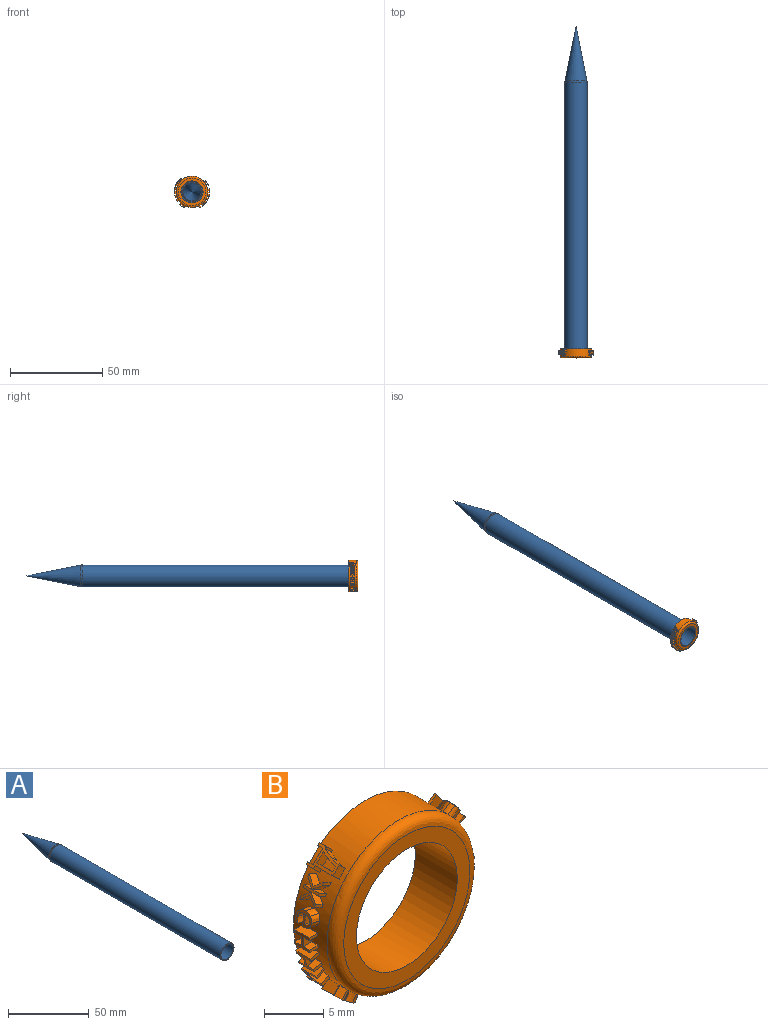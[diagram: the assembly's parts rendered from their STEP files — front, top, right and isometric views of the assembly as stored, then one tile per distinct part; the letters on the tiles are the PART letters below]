
ASSEMBLY  parts=2 mates=1
PART A: 8 faces, bbox 12x180x12 mm
  f0: cylinder r=5.5mm len=150mm, axis (0,1,0), area 5183.6mm2, adj f2,f4
  f1: cylinder r=6mm len=149.51mm, axis (0,1,0), area 5636.2mm2, adj f2,f5
  f2: plane 12x12mm, normal (0,-1,0), area 18.1mm2, adj f0,f1
  f3: cone r=6mm half-angle=11.3deg, axis (0,-1,0), area 558.2mm2, adj f5
  f4: plane 11x11mm, normal (0,-1,0), area 17.5mm2, adj f0,f6
  f5: torus R=1mm, axis (0,-1,0), area 37mm2, adj f1,f3
  f6: torus R=1mm, axis (0,-1,0), area 9.1mm2, adj f4,f7
  f7: cone r=5.02mm half-angle=11.3deg, axis (0,-1,0), area 388.1mm2, adj f6
PART B: 300 faces, bbox 19x5x17.5 mm
  f0: plane 2.34x0.87mm, normal (0.87,0,0.49), area 2.3mm2, adj f1,f9,f10,f32
  f1: plane 1.01x0.73mm, normal (0,-1,0), area 0.3mm2, adj f0,f2,f10,f32
  f2: plane 2.36x0.87mm, normal (-0.87,0,-0.49), area 2.4mm2, adj f1,f3,f10,f32
  f3: extruded ~0.92x0.56mm, area 0.3mm2, adj f2,f4,f10,f32
  f4: extruded ~1x0.7mm, area 0.3mm2, adj f3,f5,f10,f32
  f5: extruded ~1x0.7mm, area 0.2mm2, adj f4,f6,f10,f32
  f6: plane 0.88x0.49mm, normal (-0.87,0,-0.49), area 0.2mm2, adj f5,f7,f10,f32
  f7: extruded ~1x0.7mm, area 0.2mm2, adj f6,f8,f10,f32
  f8: extruded ~1.1x0.88mm, area 0.5mm2, adj f7,f9,f10,f32
  f9: extruded ~0.95x0.62mm, area 0.5mm2, adj f0,f8,f10,f32
  f10: cylinder r=9.5mm len=2.98mm, axis (0,1,0), area 0.9mm2, adj f0,f1,f2,f3,f4,f5,f6,f7
  f11: extruded ~0.95x0.86mm, area 0.3mm2, adj f12,f24,f30,f32
  f12: extruded ~0.97x0.88mm, area 0.3mm2, adj f11,f13,f30,f32
  f13: extruded ~1.18x1.13mm, area 0.7mm2, adj f12,f14,f30,f32
  f14: extruded ~0.93x0.83mm, area 0.7mm2, adj f13,f15,f30,f32
  f15: extruded ~0.92x0.82mm, area 0.7mm2, adj f14,f16,f30,f32
  f16: extruded ~1.14x1.09mm, area 0.6mm2, adj f15,f17,f30,f32
  f17: extruded ~1.12x1.06mm, area 0.6mm2, adj f16,f18,f30,f32
  f18: extruded ~0.9x0.8mm, area 0.6mm2, adj f17,f19,f30,f32
  f19: plane 0.77x0.64mm, normal (0.77,0,0.64), area 0.2mm2, adj f18,f20,f30,f32
  f20: plane 1.57x1.56mm, normal (0,1,0), area 1.2mm2, adj f19,f21,f30,f32
  f21: extruded ~0.87x0.77mm, area 0.5mm2, adj f20,f22,f30,f32
  f22: extruded ~1.04x0.97mm, area 0.5mm2, adj f21,f23,f30,f32
  f23: extruded ~1.15x1.09mm, area 0.6mm2, adj f22,f24,f30,f32
  f24: plane 0.77x0.64mm, normal (0.77,0,0.64), area 0.2mm2, adj f11,f23,f30,f32
  f25: plane 1.36x1.35mm, normal (0,-1,0), area 0.9mm2, adj f26,f29,f30,f31
  f26: extruded ~0.87x0.76mm, area 0.4mm2, adj f25,f27,f30,f31
  f27: extruded ~0.99x0.91mm, area 0.4mm2, adj f26,f28,f30,f31
  f28: extruded ~0.98x0.89mm, area 0.4mm2, adj f27,f29,f30,f31
  f29: extruded ~0.84x0.73mm, area 0.4mm2, adj f25,f28,f30,f31
  f30: cylinder r=9.5mm len=1.83mm, axis (0,1,0), area 1.2mm2, adj f11,f12,f13,f14,f15,f16,f17,f18
  f31: cylinder r=8.5mm len=0.71mm, axis (0,1,0), area 0.4mm2, adj f25,f26,f27,f28,f29
  f32: cylinder r=8.5mm len=17mm, axis (0,1,0), area 190.6mm2, adj f0,f1,f2,f3,f4,f5,f6,f7
  f33: plane 1.21x0.79mm, normal (0.61,0,0.79), area 1.2mm2, adj f32,f34,f51,f60
  f34: plane 0.91x0.78mm, normal (0,1,0), area 0.2mm2, adj f32,f33,f35,f60
  f35: plane 0.82x0.66mm, normal (-0.6,0.21,-0.77), area 0.3mm2, adj f32,f34,f36,f60
  f36: plane 0.8x0.62mm, normal (0,1,0), area 0mm2, adj f32,f35,f37,f60
  f37: extruded ~0.96x0.83mm, area 0.4mm2, adj f32,f36,f38,f60
  f38: extruded ~0.99x0.87mm, area 0.3mm2, adj f32,f37,f39,f60
  f39: extruded ~1.06x0.95mm, area 0.4mm2, adj f32,f38,f40,f60
  f40: extruded ~0.89x0.74mm, area 0.4mm2, adj f32,f39,f41,f60
  f41: extruded ~1.34x1.31mm, area 1.2mm2, adj f32,f40,f42,f60
  f42: plane 0.97x0.85mm, normal (-0.02,-1,-0.03), area 0.3mm2, adj f32,f41,f43,f60
  f43: plane 0.79x0.61mm, normal (-0.61,0,-0.79), area 0.1mm2, adj f32,f42,f44,f60
  f44: extruded ~0.85x0.68mm, area 0.3mm2, adj f32,f43,f45,f60
  f45: extruded ~0.97x0.84mm, area 0.3mm2, adj f32,f44,f46,f60
  f46: extruded ~1.11x1.01mm, area 0.5mm2, adj f32,f45,f47,f60
  f47: plane 0.85x0.67mm, normal (-0.57,0.37,-0.73), area 0.2mm2, adj f32,f46,f48,f60
  f48: extruded ~0.98x0.85mm, area 0.3mm2, adj f32,f47,f49,f60
  f49: extruded ~0.99x0.86mm, area 0.3mm2, adj f32,f48,f50,f60
  f50: extruded ~1.09x0.99mm, area 0.5mm2, adj f32,f49,f51,f60
  f51: extruded ~0.9x0.74mm, area 0.5mm2, adj f32,f33,f50,f60
  f52: extruded ~0.88x0.73mm, area 0.3mm2, adj f53,f59,f60,f61
  f53: extruded ~1.08x0.98mm, area 0.5mm2, adj f52,f54,f60,f61
  f54: plane 0.95x0.83mm, normal (0.02,1,0.03), area 0.3mm2, adj f53,f55,f60,f61
  f55: plane 0.79x0.61mm, normal (-0.61,0,-0.79), area 0.2mm2, adj f54,f56,f60,f61
  f56: extruded ~0.88x0.73mm, area 0.4mm2, adj f55,f57,f60,f61
  f57: extruded ~1.03x0.92mm, area 0.4mm2, adj f56,f58,f60,f61
  f58: extruded ~0.95x0.81mm, area 0.3mm2, adj f57,f59,f60,f61
  f59: extruded ~0.85x0.68mm, area 0.2mm2, adj f52,f58,f60,f61
  f60: cylinder r=9.5mm len=1.83mm, axis (0,1,0), area 1.2mm2, adj f33,f34,f35,f36,f37,f38,f39,f40
  f61: cylinder r=8.5mm len=0.69mm, axis (0,1,0), area 0.4mm2, adj f52,f53,f54,f55,f56,f57,f58,f59
  f62: extruded ~0.99x0.58mm, area 0.5mm2, adj f32,f63,f78,f79
  f63: extruded ~1.13x0.87mm, area 0.5mm2, adj f32,f62,f64,f79
  f64: extruded ~1.05x0.72mm, area 0.3mm2, adj f32,f63,f65,f79
  f65: extruded ~1.01x0.64mm, area 0.3mm2, adj f32,f64,f66,f79
  f66: plane 0.91x0.43mm, normal (0,-1,0), area 0mm2, adj f32,f65,f67,f79
  f67: plane 0.93x0.46mm, normal (0.42,-0.18,0.89), area 0.2mm2, adj f32,f66,f68,f79
  f68: plane 1.01x0.61mm, normal (0,-1,0), area 0.2mm2, adj f32,f67,f69,f79
  f69: plane 1.77x0.91mm, normal (-0.42,0,-0.91), area 1.8mm2, adj f32,f68,f70,f79
  f70: plane 1.04x0.66mm, normal (0,1,0), area 0.3mm2, adj f32,f69,f71,f79
  f71: plane 0.93x0.91mm, normal (0.42,0,0.91), area 0.9mm2, adj f32,f70,f72,f79
  f72: extruded ~0.97x0.54mm, area 0.5mm2, adj f32,f71,f73,f79
  f73: extruded ~1.08x0.79mm, area 0.4mm2, adj f32,f72,f74,f79
  f74: extruded ~1.05x0.71mm, area 0.3mm2, adj f32,f73,f75,f79
  f75: extruded ~0.95x0.51mm, area 0.3mm2, adj f32,f74,f76,f79
  f76: plane 1.14x0.91mm, normal (-0.42,0,-0.91), area 1.1mm2, adj f32,f75,f77,f79
  f77: plane 1x0.67mm, normal (0,1,0), area 0.3mm2, adj f32,f76,f78,f79
  f78: plane 1.15x0.91mm, normal (0.42,0,0.91), area 1.2mm2, adj f32,f62,f77,f79
  f79: cylinder r=9.5mm len=1.8mm, axis (0,1,0), area 1.1mm2, adj f62,f63,f64,f65,f66,f67,f68,f69
  f80: extruded ~1.03x0.49mm, area 0.5mm2, adj f32,f81,f96,f97
  f81: extruded ~1.1x0.68mm, area 0.5mm2, adj f32,f80,f82,f97
  f82: extruded ~1.05x0.53mm, area 0.3mm2, adj f32,f81,f83,f97
  f83: extruded ~1.03x0.43mm, area 0.3mm2, adj f32,f82,f84,f97
  f84: plane 0.98x0.21mm, normal (0,-1,0), area 0mm2, adj f32,f83,f85,f97
  f85: plane 0.99x0.24mm, normal (0.2,-0.18,0.96), area 0.2mm2, adj f32,f84,f86,f97
  f86: plane 1.04x0.41mm, normal (0,-1,0), area 0.2mm2, adj f32,f85,f87,f97
  f87: plane 1.77x0.98mm, normal (-0.2,0,-0.98), area 1.8mm2, adj f32,f86,f88,f97
  f88: plane 1.05x0.46mm, normal (0,1,0), area 0.3mm2, adj f32,f87,f89,f97
  f89: plane 0.98x0.93mm, normal (0.2,0,0.98), area 0.9mm2, adj f32,f88,f90,f97
  f90: extruded ~1.01x0.5mm, area 0.5mm2, adj f32,f89,f91,f97
  f91: extruded ~1.07x0.6mm, area 0.4mm2, adj f32,f90,f92,f97
  f92: extruded ~1.05x0.51mm, area 0.3mm2, adj f32,f91,f93,f97
  f93: extruded ~1.01x0.32mm, area 0.3mm2, adj f32,f92,f94,f97
  f94: plane 1.14x0.98mm, normal (-0.2,0,-0.98), area 1.1mm2, adj f32,f93,f95,f97
  f95: plane 1.02x0.47mm, normal (0,1,0), area 0.3mm2, adj f32,f94,f96,f97
  f96: plane 1.15x0.98mm, normal (0.2,0,0.98), area 1.2mm2, adj f32,f80,f95,f97
  f97: cylinder r=9.5mm len=1.8mm, axis (0,1,0), area 1.1mm2, adj f80,f81,f82,f83,f84,f85,f86,f87
  f98: plane 1.77x1mm, normal (-0.04,0,-1), area 1.8mm2, adj f32,f99,f101,f102
  f99: plane 1.01x0.31mm, normal (0,1,0), area 0.3mm2, adj f32,f98,f100,f102
  f100: plane 1.77x1mm, normal (0.04,0,1), area 1.8mm2, adj f32,f99,f101,f102
  f101: plane 1.01x0.31mm, normal (0,-1,0), area 0.3mm2, adj f32,f98,f100,f102
  f102: cylinder r=9.5mm len=1.77mm, axis (0,1,0), area 0.5mm2, adj f98,f99,f100,f101
  f103: extruded ~1.01x0.15mm, area 0.1mm2, adj f32,f104,f110,f111
  f104: extruded ~1x0.13mm, area 0.1mm2, adj f32,f103,f105,f111
  f105: extruded ~1x0.13mm, area 0.1mm2, adj f32,f104,f106,f111
  f106: extruded ~1.01x0.15mm, area 0.1mm2, adj f32,f105,f107,f111
  f107: extruded ~1x0.15mm, area 0.1mm2, adj f32,f106,f108,f111
  f108: extruded ~1x0.13mm, area 0.1mm2, adj f32,f107,f109,f111
  f109: extruded ~1x0.13mm, area 0.1mm2, adj f32,f108,f110,f111
  f110: extruded ~1x0.15mm, area 0.1mm2, adj f32,f103,f109,f111
  f111: cylinder r=9.5mm len=0.36mm, axis (0,1,0), area 0.1mm2, adj f103,f104,f105,f106,f107,f108,f109,f110
  f112: extruded ~1.04x0.39mm, area 0.3mm2, adj f32,f113,f125,f131
  f113: extruded ~1.04x0.42mm, area 0.3mm2, adj f32,f112,f114,f131
  f114: extruded ~1.08x0.73mm, area 0.7mm2, adj f32,f113,f115,f131
  f115: extruded ~1.04x0.66mm, area 0.7mm2, adj f32,f114,f116,f131
  f116: extruded ~1.04x0.68mm, area 0.7mm2, adj f32,f115,f117,f131
  f117: extruded ~1.08x0.68mm, area 0.6mm2, adj f32,f116,f118,f131
  f118: extruded ~1.07x0.64mm, area 0.6mm2, adj f32,f117,f119,f131
  f119: extruded ~1.03x0.58mm, area 0.6mm2, adj f32,f118,f120,f131
  f120: plane 1x0.17mm, normal (-0.12,0,0.99), area 0.2mm2, adj f32,f119,f121,f131
  f121: plane 1.33x1.16mm, normal (0,1,0), area 1.2mm2, adj f32,f120,f122,f131
  f122: extruded ~1.02x0.47mm, area 0.5mm2, adj f32,f121,f123,f131
  f123: extruded ~1.05x0.54mm, area 0.5mm2, adj f32,f122,f124,f131
  f124: extruded ~1.08x0.68mm, area 0.6mm2, adj f32,f123,f125,f131
  f125: plane 1x0.24mm, normal (-0.12,0,0.99), area 0.2mm2, adj f32,f112,f124,f131
  f126: plane 1.1x1.04mm, normal (0,-1,0), area 0.9mm2, adj f127,f130,f131,f132
  f127: extruded ~1.02x0.38mm, area 0.4mm2, adj f126,f128,f131,f132
  f128: extruded ~1.04x0.46mm, area 0.4mm2, adj f127,f129,f131,f132
  f129: extruded ~1.04x0.44mm, area 0.4mm2, adj f128,f130,f131,f132
  f130: extruded ~1.01x0.39mm, area 0.4mm2, adj f126,f129,f131,f132
  f131: cylinder r=9.5mm len=1.83mm, axis (0,1,0), area 1.2mm2, adj f112,f113,f114,f115,f116,f117,f118,f119
  f132: cylinder r=8.5mm len=0.92mm, axis (0,1,0), area 0.4mm2, adj f126,f127,f128,f129,f130
  f133: plane 1.17x1mm, normal (0.26,-0.79,-0.55), area 0.8mm2, adj f32,f134,f141,f142
  f134: plane 0.96x0.56mm, normal (0.34,0.61,-0.71), area 0.2mm2, adj f32,f133,f135,f142
  f135: extruded ~1.07x0.78mm, area 0.5mm2, adj f32,f134,f136,f142
  f136: extruded ~0.94x0.5mm, area 0.1mm2, adj f32,f135,f137,f142
  f137: extruded ~0.91x0.44mm, area 0.4mm2, adj f32,f136,f138,f142
  f138: plane 1.68x0.9mm, normal (0.43,0,-0.9), area 1.7mm2, adj f32,f137,f139,f142
  f139: plane 1.03x0.66mm, normal (0,1,0), area 0.3mm2, adj f32,f138,f140,f142
  f140: plane 2.36x0.9mm, normal (-0.43,0,0.9), area 2.4mm2, adj f32,f139,f141,f142
  f141: plane 1.01x0.63mm, normal (0,-1,0), area 0.2mm2, adj f32,f133,f140,f142
  f142: cylinder r=9.5mm len=2.36mm, axis (0,1,0), area 0.8mm2, adj f133,f134,f135,f136,f137,f138,f139,f140
  f143: plane 0.8x0.6mm, normal (-0.6,0,0.8), area 0mm2, adj f32,f144,f162,f163
  f144: plane 1.1x1.02mm, normal (-0.42,0.71,0.56), area 0.7mm2, adj f32,f143,f145,f163
  f145: extruded ~1.1x0.98mm, area 0.7mm2, adj f32,f144,f146,f163
  f146: extruded ~0.89x0.7mm, area 0.5mm2, adj f32,f145,f147,f163
  f147: extruded ~0.93x0.76mm, area 0.5mm2, adj f32,f146,f148,f163
  f148: extruded ~1.12x1.02mm, area 0.6mm2, adj f32,f147,f149,f163
  f149: extruded ~1.25x1.19mm, area 0.8mm2, adj f32,f148,f150,f163
  f150: plane 0.88x0.72mm, normal (0.47,0.61,-0.63), area 0.2mm2, adj f32,f149,f151,f163
  f151: extruded ~0.99x0.84mm, area 0.3mm2, adj f32,f150,f152,f163
  f152: extruded ~0.97x0.82mm, area 0.3mm2, adj f32,f151,f153,f163
  f153: extruded ~1x0.85mm, area 0.3mm2, adj f32,f152,f154,f163
  f154: extruded ~0.88x0.69mm, area 0.3mm2, adj f32,f153,f155,f163
  f155: extruded ~0.83x0.63mm, area 0.3mm2, adj f32,f154,f156,f163
  f156: extruded ~0.89x0.71mm, area 0.3mm2, adj f32,f155,f157,f163
  f157: extruded ~1.03x0.9mm, area 0.6mm2, adj f32,f156,f158,f163
  f158: plane 1.15x1.12mm, normal (0.42,-0.71,-0.57), area 0.9mm2, adj f32,f157,f159,f163
  f159: plane 0.81x0.6mm, normal (0.6,0,-0.8), area 0.2mm2, adj f32,f158,f160,f163
  f160: plane 1.85x1.73mm, normal (0,1,0), area 1.6mm2, adj f32,f159,f161,f163
  f161: plane 0.81x0.6mm, normal (-0.6,0,0.8), area 0.2mm2, adj f32,f160,f162,f163
  f162: plane 1.56x1.54mm, normal (0,-1,0), area 1.2mm2, adj f32,f143,f161,f163
  f163: cylinder r=9.5mm len=2.39mm, axis (0,1,0), area 1.2mm2, adj f143,f144,f145,f146,f147,f148,f149,f150
  f164: plane 0.93x0.91mm, normal (0,-1,0), area 0.3mm2, adj f32,f165,f176,f182
  f165: plane 0.86x0.72mm, normal (-0.7,0,-0.72), area 0.9mm2, adj f32,f164,f166,f182
  f166: plane 0.91x0.88mm, normal (0,1,0), area 0.3mm2, adj f32,f165,f167,f182
  f167: plane 0.72x0.7mm, normal (0.7,0,0.72), area 0.6mm2, adj f32,f166,f168,f182
  f168: plane 1.88x1.86mm, normal (0,1,0), area 1.6mm2, adj f32,f167,f169,f182
  f169: plane 0.72x0.7mm, normal (-0.7,0,-0.72), area 0.6mm2, adj f32,f168,f170,f182
  f170: plane 0.93x0.87mm, normal (0,1,0), area 0.3mm2, adj f32,f169,f171,f182
  f171: plane 0.86x0.72mm, normal (0.7,0,0.72), area 0.9mm2, adj f32,f170,f172,f182
  f172: plane 0.87x0.82mm, normal (0,-1,0), area 0.2mm2, adj f32,f171,f173,f182
  f173: extruded ~1.04x1.03mm, area 1.1mm2, adj f32,f172,f174,f182
  f174: extruded ~1.09x0.86mm, area 1.1mm2, adj f32,f173,f175,f182
  f175: plane 1.47x1.44mm, normal (0,-1,0), area 1.1mm2, adj f32,f174,f176,f182
  f176: plane 2.11x0.72mm, normal (-0.7,0,-0.72), area 2.1mm2, adj f32,f164,f175,f182
  f177: extruded ~0.94x0.86mm, area 1mm2, adj f178,f181,f182,f183
  f178: plane 1.09x1.09mm, normal (0,1,0), area 0.5mm2, adj f177,f179,f182,f183
  f179: plane 1.86x0.72mm, normal (0.7,0,0.72), area 1.9mm2, adj f178,f180,f182,f183
  f180: plane 1.51x1.49mm, normal (0,-1,0), area 1.1mm2, adj f179,f181,f182,f183
  f181: extruded ~1x0.99mm, area 1mm2, adj f177,f180,f182,f183
  f182: cylinder r=9.5mm len=2.97mm, axis (0,1,0), area 2.2mm2, adj f164,f165,f166,f167,f168,f169,f170,f171
  f183: cylinder r=8.5mm len=1.86mm, axis (0,1,0), area 1.5mm2, adj f177,f178,f179,f180,f181
  f184: plane 1.27x1.09mm, normal (-0.35,-0.65,-0.68), area 1.1mm2, adj f32,f185,f201,f202
  f185: plane 0.89x0.86mm, normal (0.46,0,0.89), area 0.9mm2, adj f32,f184,f186,f202
  f186: plane 1.01x0.68mm, normal (0,-1,0), area 0.2mm2, adj f32,f185,f187,f202
  f187: plane 0.89x0.86mm, normal (-0.46,0,-0.89), area 0.9mm2, adj f32,f186,f188,f202
  f188: plane 1.2x1.12mm, normal (0.35,-0.65,0.68), area 1.1mm2, adj f32,f187,f189,f202
  f189: plane 1x0.73mm, normal (0,-1,0), area 0.3mm2, adj f32,f188,f190,f202
  f190: plane 1.18x1.14mm, normal (-0.35,0.65,-0.67), area 1.1mm2, adj f32,f189,f191,f202
  f191: plane 1.21x1.2mm, normal (-0.34,-0.66,-0.67), area 1.2mm2, adj f32,f190,f192,f202
  f192: plane 1.01x0.75mm, normal (0,1,0), area 0.3mm2, adj f32,f191,f193,f202
  f193: plane 1.22x1.17mm, normal (0.35,0.66,0.67), area 1.2mm2, adj f32,f192,f194,f202
  f194: plane 0.9x0.89mm, normal (-0.46,0,-0.89), area 0.9mm2, adj f32,f193,f195,f202
  f195: plane 1.01x0.68mm, normal (0,1,0), area 0.2mm2, adj f32,f194,f196,f202
  f196: plane 0.9x0.89mm, normal (0.46,0,0.89), area 0.9mm2, adj f32,f195,f197,f202
  f197: plane 1.3x1.13mm, normal (-0.35,0.66,-0.67), area 1.2mm2, adj f32,f196,f198,f202
  f198: plane 1.07x0.72mm, normal (0,1,0), area 0.3mm2, adj f32,f197,f199,f202
  f199: plane 1.34x1.14mm, normal (0.34,-0.66,0.67), area 1.2mm2, adj f32,f198,f200,f202
  f200: plane 1.3x1.08mm, normal (0.35,0.65,0.67), area 1.1mm2, adj f32,f199,f201,f202
  f201: plane 1.06x0.71mm, normal (0,-1,0), area 0.3mm2, adj f32,f184,f200,f202
  f202: cylinder r=9.5mm len=2.14mm, axis (0,1,0), area 1.5mm2, adj f184,f185,f186,f187,f188,f189,f190,f191
  f203: extruded ~1.05x0.47mm, area 0.3mm2, adj f32,f204,f216,f222
  f204: extruded ~1.05x0.51mm, area 0.3mm2, adj f32,f203,f205,f222
  f205: extruded ~1.12x0.82mm, area 0.7mm2, adj f32,f204,f206,f222
  f206: extruded ~1.04x0.66mm, area 0.7mm2, adj f32,f205,f207,f222
  f207: extruded ~1.04x0.68mm, area 0.7mm2, adj f32,f206,f208,f222
  f208: extruded ~1.11x0.76mm, area 0.6mm2, adj f32,f207,f209,f222
  f209: extruded ~1.1x0.72mm, area 0.6mm2, adj f32,f208,f210,f222
  f210: extruded ~1.03x0.58mm, area 0.6mm2, adj f32,f209,f211,f222
  f211: plane 0.98x0.21mm, normal (-0.21,0,-0.98), area 0.2mm2, adj f32,f210,f212,f222
  f212: plane 1.4x1.22mm, normal (0,1,0), area 1.2mm2, adj f32,f211,f213,f222
  f213: extruded ~1.02x0.47mm, area 0.5mm2, adj f32,f212,f214,f222
  f214: extruded ~1.07x0.62mm, area 0.5mm2, adj f32,f213,f215,f222
  f215: extruded ~1.12x0.76mm, area 0.6mm2, adj f32,f214,f216,f222
  f216: plane 0.98x0.24mm, normal (-0.21,0,-0.98), area 0.2mm2, adj f32,f203,f215,f222
  f217: plane 1.17x1.11mm, normal (0,-1,0), area 0.9mm2, adj f218,f221,f222,f223
  f218: extruded ~1.02x0.38mm, area 0.4mm2, adj f217,f219,f222,f223
  f219: extruded ~1.06x0.54mm, area 0.4mm2, adj f218,f220,f222,f223
  f220: extruded ~1.05x0.52mm, area 0.4mm2, adj f219,f221,f222,f223
  f221: extruded ~1.01x0.39mm, area 0.4mm2, adj f217,f220,f222,f223
  f222: cylinder r=9.5mm len=1.83mm, axis (0,1,0), area 1.2mm2, adj f203,f204,f205,f206,f207,f208,f209,f210
  f223: cylinder r=8.5mm len=0.9mm, axis (0,1,0), area 0.4mm2, adj f217,f218,f219,f220,f221
  f224: plane 1.01x0.29mm, normal (0,1,0), area 0.3mm2, adj f32,f225,f235,f236
  f225: plane 1x0.8mm, normal (0.02,0,-1), area 0.8mm2, adj f32,f224,f226,f236
  f226: plane 1.03x1.01mm, normal (0,1,0), area 1mm2, adj f32,f225,f227,f236
  f227: plane 1x0.8mm, normal (-0.02,0,1), area 0.8mm2, adj f32,f226,f228,f236
  f228: plane 1.03x0.29mm, normal (0,1,0), area 0.3mm2, adj f32,f227,f229,f236
  f229: plane 1.77x1mm, normal (0.02,0,-1), area 1.8mm2, adj f32,f228,f230,f236
  f230: plane 1.03x0.29mm, normal (0,-1,0), area 0.3mm2, adj f32,f229,f231,f236
  f231: plane 1x0.74mm, normal (-0.02,0,1), area 0.7mm2, adj f32,f230,f232,f236
  f232: plane 1.03x1.01mm, normal (0,-1,0), area 1mm2, adj f32,f231,f233,f236
  f233: plane 1x0.74mm, normal (0.02,0,-1), area 0.7mm2, adj f32,f232,f234,f236
  f234: plane 1.01x0.29mm, normal (0,-1,0), area 0.3mm2, adj f32,f233,f235,f236
  f235: plane 1.77x1mm, normal (-0.02,0,1), area 1.8mm2, adj f32,f224,f234,f236
  f236: cylinder r=9.5mm len=1.77mm, axis (0,1,0), area 1.2mm2, adj f224,f225,f226,f227,f228,f229,f230,f231
  f237: plane 1.02x0.52mm, normal (0,1,0), area 0.3mm2, adj f32,f238,f248,f249
  f238: plane 0.97x0.8mm, normal (0.26,0,-0.97), area 0.8mm2, adj f32,f237,f239,f249
  f239: plane 1.23x1.21mm, normal (0,1,0), area 1mm2, adj f32,f238,f240,f249
  f240: plane 0.97x0.8mm, normal (-0.26,0,0.97), area 0.8mm2, adj f32,f239,f241,f249
  f241: plane 1.06x0.51mm, normal (0,1,0), area 0.3mm2, adj f32,f240,f242,f249
  f242: plane 1.77x0.97mm, normal (0.26,0,-0.97), area 1.8mm2, adj f32,f241,f243,f249
  f243: plane 1.06x0.51mm, normal (0,-1,0), area 0.3mm2, adj f32,f242,f244,f249
  f244: plane 0.97x0.74mm, normal (-0.26,0,0.97), area 0.7mm2, adj f32,f243,f245,f249
  f245: plane 1.23x1.21mm, normal (0,-1,0), area 1mm2, adj f32,f244,f246,f249
  f246: plane 0.97x0.74mm, normal (0.26,0,-0.97), area 0.7mm2, adj f32,f245,f247,f249
  f247: plane 1.02x0.52mm, normal (0,-1,0), area 0.3mm2, adj f32,f246,f248,f249
  f248: plane 1.77x0.97mm, normal (-0.26,0,0.97), area 1.8mm2, adj f32,f237,f247,f249
  f249: cylinder r=9.5mm len=1.77mm, axis (0,1,0), area 1.2mm2, adj f237,f238,f239,f240,f241,f242,f243,f244
  f250: plane 1.02x0.78mm, normal (0,1,0), area 0.3mm2, adj f32,f251,f263,f264
  f251: plane 1.5x1.34mm, normal (0.4,0.54,-0.74), area 1.8mm2, adj f32,f250,f252,f264
  f252: plane 0.88x0.49mm, normal (-0.48,-0.04,0.88), area 0.2mm2, adj f32,f251,f253,f264
  f253: plane 0.88x0.48mm, normal (-0.48,-0.02,0.88), area 0.2mm2, adj f32,f252,f254,f264
  f254: plane 1.08x0.88mm, normal (-0.48,0,0.88), area 1.1mm2, adj f32,f253,f255,f264
  f255: plane 1.02x0.69mm, normal (0,1,0), area 0.3mm2, adj f32,f254,f256,f264
  f256: plane 1.77x0.88mm, normal (0.48,0,-0.88), area 1.8mm2, adj f32,f255,f257,f264
  f257: plane 1.06x0.76mm, normal (0,-1,0), area 0.3mm2, adj f32,f256,f258,f264
  f258: plane 1.51x1.34mm, normal (-0.4,-0.54,0.74), area 1.8mm2, adj f32,f257,f259,f264
  f259: plane 0.88x0.48mm, normal (0.48,0.06,-0.88), area 0.1mm2, adj f32,f258,f260,f264
  f260: plane 0.88x0.49mm, normal (0.48,0.04,-0.88), area 0.3mm2, adj f32,f259,f261,f264
  f261: plane 1.12x0.88mm, normal (0.48,0,-0.88), area 1.1mm2, adj f32,f260,f262,f264
  f262: plane 0.99x0.71mm, normal (0,-1,0), area 0.3mm2, adj f32,f261,f263,f264
  f263: plane 1.77x0.88mm, normal (-0.48,0,0.88), area 1.8mm2, adj f32,f250,f262,f264
  f264: cylinder r=9.5mm len=1.77mm, axis (0,1,0), area 1.3mm2, adj f250,f251,f252,f253,f254,f255,f256,f257
  f265: plane 1.16x1.13mm, normal (-0.45,-0.79,0.41), area 0.8mm2, adj f32,f266,f273,f274
  f266: plane 0.84x0.78mm, normal (-0.59,0.61,0.53), area 0.2mm2, adj f32,f265,f267,f274
  f267: extruded ~1x0.96mm, area 0.5mm2, adj f32,f266,f268,f274
  f268: extruded ~0.79x0.73mm, area 0.1mm2, adj f32,f267,f269,f274
  f269: extruded ~0.75x0.68mm, area 0.4mm2, adj f32,f268,f270,f274
  f270: plane 1.68x0.74mm, normal (-0.74,0,0.67), area 1.7mm2, adj f32,f269,f271,f274
  f271: plane 0.91x0.87mm, normal (0,1,0), area 0.3mm2, adj f32,f270,f272,f274
  f272: plane 2.36x0.74mm, normal (0.74,0,-0.67), area 2.4mm2, adj f32,f271,f273,f274
  f273: plane 0.89x0.85mm, normal (0,-1,0), area 0.2mm2, adj f32,f265,f272,f274
  f274: cylinder r=9.5mm len=2.36mm, axis (0,1,0), area 0.8mm2, adj f265,f266,f267,f268,f269,f270,f271,f272
  f275: plane 0.86x0.52mm, normal (0.86,0,-0.52), area 0mm2, adj f32,f276,f294,f295
  f276: plane 1.13x0.95mm, normal (0.6,0.71,-0.36), area 0.7mm2, adj f32,f275,f277,f295
  f277: extruded ~1.11x0.93mm, area 0.7mm2, adj f32,f276,f278,f295
  f278: extruded ~0.93x0.63mm, area 0.5mm2, adj f32,f277,f279,f295
  f279: extruded ~0.96x0.69mm, area 0.5mm2, adj f32,f278,f280,f295
  f280: extruded ~1.14x0.97mm, area 0.6mm2, adj f32,f279,f281,f295
  f281: extruded ~1.25x1.14mm, area 0.8mm2, adj f32,f280,f282,f295
  f282: plane 0.94x0.64mm, normal (-0.67,0.61,0.41), area 0.2mm2, adj f32,f281,f283,f295
  f283: extruded ~1.02x0.78mm, area 0.3mm2, adj f32,f282,f284,f295
  f284: extruded ~1.01x0.76mm, area 0.3mm2, adj f32,f283,f285,f295
  f285: extruded ~1.02x0.79mm, area 0.3mm2, adj f32,f284,f286,f295
  f286: extruded ~0.92x0.62mm, area 0.3mm2, adj f32,f285,f287,f295
  f287: extruded ~0.88x0.56mm, area 0.3mm2, adj f32,f286,f288,f295
  f288: extruded ~0.93x0.64mm, area 0.3mm2, adj f32,f287,f289,f295
  f289: extruded ~1.05x0.84mm, area 0.6mm2, adj f32,f288,f290,f295
  f290: plane 1.21x1.03mm, normal (-0.61,-0.71,0.37), area 0.9mm2, adj f32,f289,f291,f295
  f291: plane 0.86x0.52mm, normal (-0.86,0,0.52), area 0.2mm2, adj f32,f290,f292,f295
  f292: plane 1.84x1.67mm, normal (0,1,0), area 1.6mm2, adj f32,f291,f293,f295
  f293: plane 0.86x0.52mm, normal (0.86,0,-0.52), area 0.2mm2, adj f32,f292,f294,f295
  f294: plane 1.57x1.47mm, normal (0,-1,0), area 1.2mm2, adj f32,f275,f293,f295
  f295: cylinder r=9.5mm len=2.39mm, axis (0,1,0), area 1.2mm2, adj f275,f276,f277,f278,f279,f280,f281,f282
  f296: plane 15.01x15.01mm, normal (0,-1,0), area 63.6mm2, adj f298,f299
  f297: plane 17x17mm, normal (0,1,0), area 113.9mm2, adj f32,f298
  f298: cylinder r=6mm len=12mm, axis (0,1,0), area 188.5mm2, adj f296,f297
  f299: bspline ~17.44x17.44mm, area 83.4mm2, adj f32,f296
PLACE A t=(18.09,244.12,129.24)mm
PLACE B t=(18.09,99.12,129.24)mm
MATE fastened A.f1 <-> B.f298  axis (0,1,0) through (18.09,94.12,129.24)mm
